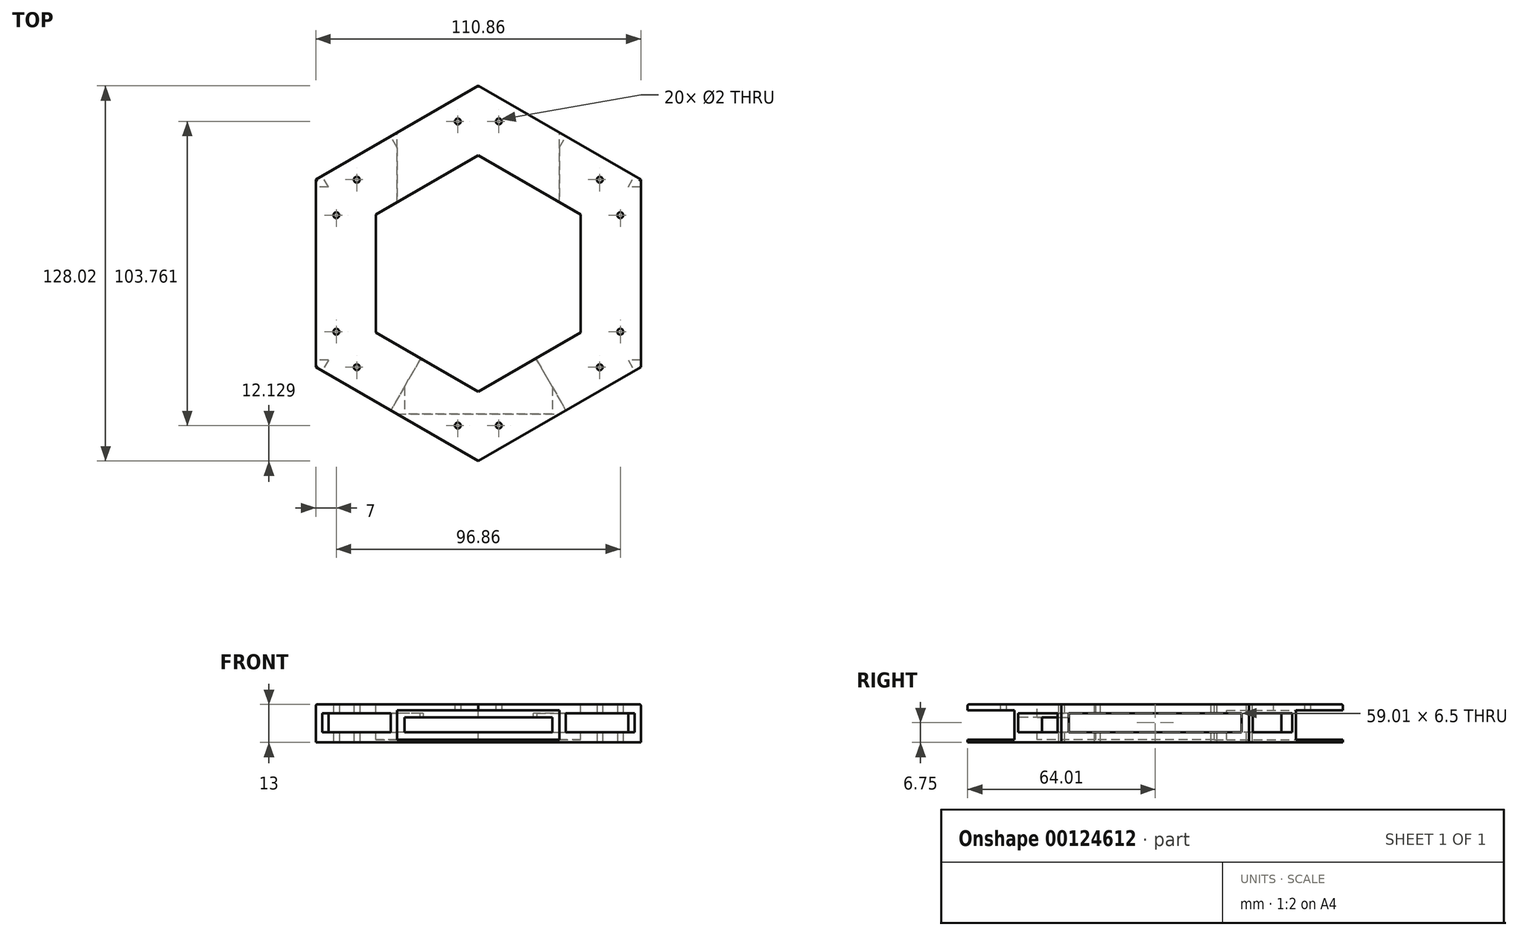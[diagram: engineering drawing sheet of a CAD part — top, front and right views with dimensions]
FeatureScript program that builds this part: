
annotation { "Feature Type Name" : "Feature", "Feature Type Description" : "" }
export const myFeature = defineFeature(function(context is Context, id is Id, definition is map)
    precondition{}
    {
        {
            var Q0;
            Q0=qCreatedBy(makeId("Top.planeOp"),FACE);
            var sketch = newSketch(context, id + "F0", { "sketchPlane" : qUnion([Q0])});
            skCircle(sketch, "E0.cCircle", {"center": v(0, 0) * mm, "radius": 55.43 * mm, "construction": true});
            skLineSegment(sketch, "E0.0", {"start": v(-55.43, -32) * mm, "end": v(-55.43, 32) * mm});
            skLineSegment(sketch, "E0.1", {"start": v(-55.43, 32) * mm, "end": v(0, 64) * mm});
            skLineSegment(sketch, "E0.2", {"start": v(0, 64) * mm, "end": v(55.43, 32) * mm});
            skLineSegment(sketch, "E0.3", {"start": v(55.43, 32) * mm, "end": v(55.43, -32) * mm});
            skLineSegment(sketch, "E0.4", {"start": v(55.43, -32) * mm, "end": v(0, -64) * mm});
            skLineSegment(sketch, "E0.5", {"start": v(0, -64) * mm, "end": v(-55.43, -32) * mm});
            skPoint(sketch, "E0.0.midPoint", {"position": v(-55.43, 0) * mm});
            skLineSegment(sketch, "E1", {"start": v(-55.43, -32) * mm, "end": v(0, 0) * mm});
            skLineSegment(sketch, "E2", {"start": v(-55.43, 32) * mm, "end": v(0, 0) * mm});
            skLineSegment(sketch, "E3.0", {"start": v(-48.43, -19.88) * mm, "end": v(-48.43, 19.88) * mm});
            skLineSegment(sketch, "E3.1", {"start": v(-48.43, -19.88) * mm, "end": v(-14, 0) * mm});
            skLineSegment(sketch, "E3.2", {"start": v(-48.43, 19.88) * mm, "end": v(-14, 0) * mm});
            skCircle(sketch, "E4", {"center": v(-48.43, -19.88) * mm, "radius": 1 * mm});
            skCircle(sketch, "E5", {"center": v(-48.43, 19.88) * mm, "radius": 1 * mm});
            skCircle(sketch, "E6.1.0", {"center": v(-7, -51.88) * mm, "radius": 1 * mm});
            skCircle(sketch, "E6.1.1", {"center": v(-41.43, -32) * mm, "radius": 1 * mm});
            skCircle(sketch, "E6.2.0", {"center": v(41.43, -32) * mm, "radius": 1 * mm});
            skCircle(sketch, "E6.2.1", {"center": v(7, -51.88) * mm, "radius": 1 * mm});
            skCircle(sketch, "E6.3.0", {"center": v(48.43, 19.88) * mm, "radius": 1 * mm});
            skCircle(sketch, "E6.3.1", {"center": v(48.43, -19.88) * mm, "radius": 1 * mm});
            skCircle(sketch, "E6.4.0", {"center": v(7, 51.88) * mm, "radius": 1 * mm});
            skCircle(sketch, "E6.4.1", {"center": v(41.43, 32) * mm, "radius": 1 * mm});
            skCircle(sketch, "E6.5.0", {"center": v(-41.43, 32) * mm, "radius": 1 * mm});
            skCircle(sketch, "E6.5.1", {"center": v(-7, 51.88) * mm, "radius": 1 * mm});
            skSolve(sketch);
        }
        {
            var Q0;
            Q0=makeQuery(id+"F0.imprint","IMPRINT",FACE,{"disambiguationData":[TD([[makeQuery(id+"F0.imprint","IMPRINT",EDGE,{"derivedFrom":sQuery(id+"F0.wireOp",EDGE,"E0.1")}),-1.0]])]});
            var Q1;
            {var subQ0=sQuery(id+"F0.wireOp",EDGE,"E4");var subQ1=sQuery(id+"F0.wireOp",EDGE,"E3.0");var subQ2=makeQuery(id+"F0.imprint","INTERSECT",VERTEX,{"derivedFrom":[subQ1,subQ0]});Q1=makeQuery(id+"F0.imprint","IMPRINT",FACE,{"disambiguationData":[TD([[makeQuery(id+"F0.imprint","IMPRINT",EDGE,{"disambiguationData":[TD([[subQ2,-1.0]])],"derivedFrom":subQ1}),-1.0]])]});}
            var Q2;
            Q2=makeQuery(id+"F0.imprint","IMPRINT",FACE,{"disambiguationData":[TD([[makeQuery(id+"F0.imprint","IMPRINT",EDGE,{"derivedFrom":sQuery(id+"F0.wireOp",EDGE,"E0.0")}),-1.0]])]});
            extrude(context, id + "F1", {"entities" : qUnion([Q0, Q1, Q2]), "depth" : 2 * mm});
        }
        {
            var Q0;
            Q0=makeQuery(id+"F1.opExtrude","CAP_EDGE",EDGE,{"disambiguationData":[OSD([sQuery(id+"F0.wireOp",EDGE,"E0.0")])],"isStart":false});
            var Q1;
            Q1=makeQuery(id+"F1.opExtrude","CAP_EDGE",EDGE,{"disambiguationData":[OSD([sQuery(id+"F0.wireOp",EDGE,"E0.5")])],"isStart":false});
            var Q2;
            Q2=makeQuery(id+"F1.opExtrude","CAP_EDGE",EDGE,{"disambiguationData":[OSD([sQuery(id+"F0.wireOp",EDGE,"E0.1")])],"isStart":false});
            var Q3;
            Q3=makeQuery(id+"F1.opExtrude","CAP_EDGE",EDGE,{"disambiguationData":[OSD([sQuery(id+"F0.wireOp",EDGE,"E0.2")])],"isStart":false});
            var Q4;
            Q4=makeQuery(id+"F1.opExtrude","CAP_EDGE",EDGE,{"disambiguationData":[OSD([sQuery(id+"F0.wireOp",EDGE,"E0.3")])],"isStart":false});
            var Q5;
            Q5=makeQuery(id+"F1.opExtrude","CAP_EDGE",EDGE,{"disambiguationData":[OSD([sQuery(id+"F0.wireOp",EDGE,"E0.4")])],"isStart":false});
            fillet(context, id + "F2", {"entities" : qUnion([Q0, Q1, Q2, Q3, Q4, Q5]), "radius" : 0.5 * mm, "tangentPropagation" : true, "allowEdgeOverflow" : false});
        }
        {
            var Q0;
            Q0=makeQuery(id+"F1.opExtrude","CAP_FACE",FACE,{"disambiguationData":[OSD([sQuery(id+"F0.wireOp",EDGE,"E0.0"),sQuery(id+"F0.wireOp",EDGE,"E0.1"),sQuery(id+"F0.wireOp",EDGE,"E0.2"),sQuery(id+"F0.wireOp",EDGE,"E0.3"),sQuery(id+"F0.wireOp",EDGE,"E0.4"),sQuery(id+"F0.wireOp",EDGE,"E0.5"),sQuery(id+"F0.wireOp",EDGE,"E4"),sQuery(id+"F0.wireOp",EDGE,"E5"),sQuery(id+"F0.wireOp",EDGE,"E6.1.0"),sQuery(id+"F0.wireOp",EDGE,"E6.1.1"),sQuery(id+"F0.wireOp",EDGE,"E6.2.0"),sQuery(id+"F0.wireOp",EDGE,"E6.2.1"),sQuery(id+"F0.wireOp",EDGE,"E6.3.0"),sQuery(id+"F0.wireOp",EDGE,"E6.3.1"),sQuery(id+"F0.wireOp",EDGE,"E6.4.0"),sQuery(id+"F0.wireOp",EDGE,"E6.4.1"),sQuery(id+"F0.wireOp",EDGE,"E6.5.0"),sQuery(id+"F0.wireOp",EDGE,"E6.5.1")])],"isStart":false});
            var sketch = newSketch(context, id + "F3", { "sketchPlane" : qUnion([Q0])});
            skLineSegment(sketch, "E7.0", {"start": v(34.93, 20.17) * mm, "end": v(0, 40.33) * mm});
            skLineSegment(sketch, "E7.1", {"start": v(-34.93, 20.17) * mm, "end": v(-34.93, -20.17) * mm});
            skLineSegment(sketch, "E7.2", {"start": v(-34.93, -20.17) * mm, "end": v(0, -40.33) * mm});
            skLineSegment(sketch, "E7.3", {"start": v(0, 40.33) * mm, "end": v(-34.93, 20.17) * mm});
            skLineSegment(sketch, "E7.4", {"start": v(0, -40.33) * mm, "end": v(34.93, -20.17) * mm});
            skLineSegment(sketch, "E7.5", {"start": v(34.93, -20.17) * mm, "end": v(34.93, 20.17) * mm});
            skLineSegment(sketch, "E8.0", {"start": v(0, -69.2) * mm, "end": v(59.93, -34.6) * mm});
            skLineSegment(sketch, "E8.1", {"start": v(59.93, 34.6) * mm, "end": v(0, 69.2) * mm});
            skLineSegment(sketch, "E8.2", {"start": v(0, 69.2) * mm, "end": v(-59.93, 34.6) * mm});
            skLineSegment(sketch, "E8.3", {"start": v(59.93, -34.6) * mm, "end": v(59.93, 34.6) * mm});
            skLineSegment(sketch, "E8.4", {"start": v(-59.93, 34.6) * mm, "end": v(-59.93, -34.6) * mm});
            skLineSegment(sketch, "E8.5", {"start": v(-59.93, -34.6) * mm, "end": v(0, -69.2) * mm});
            skSolve(sketch);
        }
        {
            var Q0;
            Q0=makeQuery(id+"F3.imprint","IMPRINT",FACE,{"disambiguationData":[TD([[makeQuery(id+"F3.imprint","IMPRINT",EDGE,{"derivedFrom":sQuery(id+"F3.wireOp",EDGE,"E7.0")}),1.0]])]});
            extrude(context, id + "F4", {"entities" : qUnion([Q0]), "operationType" : NewBodyOperationType.REMOVE, "oppositeDirection" : true, "depth" : 25 * mm});
        }
        {
            var Q0;
            Q0=makeQuery(id+"F1.opExtrude","CAP_FACE",FACE,{"disambiguationData":[OSD([sQuery(id+"F0.wireOp",EDGE,"E0.0"),sQuery(id+"F0.wireOp",EDGE,"E0.1"),sQuery(id+"F0.wireOp",EDGE,"E0.2"),sQuery(id+"F0.wireOp",EDGE,"E0.3"),sQuery(id+"F0.wireOp",EDGE,"E0.4"),sQuery(id+"F0.wireOp",EDGE,"E0.5"),sQuery(id+"F0.wireOp",EDGE,"E4"),sQuery(id+"F0.wireOp",EDGE,"E5"),sQuery(id+"F0.wireOp",EDGE,"E6.1.0"),sQuery(id+"F0.wireOp",EDGE,"E6.1.1"),sQuery(id+"F0.wireOp",EDGE,"E6.2.0"),sQuery(id+"F0.wireOp",EDGE,"E6.2.1"),sQuery(id+"F0.wireOp",EDGE,"E6.3.0"),sQuery(id+"F0.wireOp",EDGE,"E6.3.1"),sQuery(id+"F0.wireOp",EDGE,"E6.4.0"),sQuery(id+"F0.wireOp",EDGE,"E6.4.1"),sQuery(id+"F0.wireOp",EDGE,"E6.5.0"),sQuery(id+"F0.wireOp",EDGE,"E6.5.1")])],"isStart":true});
            var sketch = newSketch(context, id + "F5", { "sketchPlane" : qUnion([Q0])});
            skLineSegment(sketch, "E9", {"start": v(-17.46, 30.25) * mm, "end": v(-27.71, 48) * mm});
            skLineSegment(sketch, "E10.1.0", {"start": v(-34.93, 0) * mm, "end": v(-55.43, 0) * mm});
            skLineSegment(sketch, "E10.2.0", {"start": v(-17.46, -30.25) * mm, "end": v(-27.72, -48) * mm});
            skLineSegment(sketch, "E10.3.0", {"start": v(17.46, -30.25) * mm, "end": v(27.71, -48) * mm});
            skLineSegment(sketch, "E10.4.0", {"start": v(34.93, 0) * mm, "end": v(55.43, 0) * mm});
            skLineSegment(sketch, "E10.5.0", {"start": v(17.46, 30.25) * mm, "end": v(27.72, 48) * mm});
            skPoint(sketch, "E10.center", {"position": v(0, 0) * mm});
            skLineSegment(sketch, "E11.bottom", {"start": v(-27.71, 48) * mm, "end": v(27.71, 48) * mm});
            skLineSegment(sketch, "E11.top", {"start": v(-27.71, -48) * mm, "end": v(27.71, -48) * mm});
            skLineSegment(sketch, "E11.left", {"start": v(-27.71, 48) * mm, "end": v(-27.71, -48) * mm});
            skLineSegment(sketch, "E11.right", {"start": v(27.71, 48) * mm, "end": v(27.71, -48) * mm});
            skPoint(sketch, "E12", {"position": v(-27.71, -24.33) * mm});
            skPoint(sketch, "E13", {"position": v(-27.71, 24.33) * mm});
            skPoint(sketch, "E14", {"position": v(27.71, 24.33) * mm});
            skPoint(sketch, "E15", {"position": v(27.71, -24.33) * mm});
            skSolve(sketch);
        }
        {
            var Q0;
            {var subQ10=sQuery(id+"F5.wireOp",EDGE,"E10.1.0");Q0=makeQuery(id+"F5.imprint","IMPRINT",FACE,{"disambiguationData":[TD([[makeQuery(id+"F5.imprint","IMPRINT",EDGE,{"derivedFrom":subQ10}),-1.0]])]});}
            var Q1;
            {var subQ6=sQuery(id+"F5.wireOp",EDGE,"E10.1.0");Q1=makeQuery(id+"F5.imprint","IMPRINT",FACE,{"disambiguationData":[TD([[makeQuery(id+"F5.imprint","IMPRINT",EDGE,{"derivedFrom":subQ6}),1.0]])]});}
            var Q2;
            {var subQ10=sQuery(id+"F5.wireOp",EDGE,"E10.4.0");Q2=makeQuery(id+"F5.imprint","IMPRINT",FACE,{"disambiguationData":[TD([[makeQuery(id+"F5.imprint","IMPRINT",EDGE,{"derivedFrom":subQ10}),-1.0]])]});}
            var Q3;
            {var subQ12=sQuery(id+"F5.wireOp",EDGE,"E10.4.0");Q3=makeQuery(id+"F5.imprint","IMPRINT",FACE,{"disambiguationData":[TD([[makeQuery(id+"F5.imprint","IMPRINT",EDGE,{"derivedFrom":subQ12}),1.0]])]});}
            var Q4;
            {var subQ4=sQuery(id+"F5.wireOp",EDGE,"E9");Q4=makeQuery(id+"F5.imprint","IMPRINT",FACE,{"disambiguationData":[TD([[makeQuery(id+"F5.imprint","IMPRINT",EDGE,{"derivedFrom":subQ4}),-1.0]])]});}
            var Q5;
            {var subQ0=sQuery(id+"F5.wireOp",EDGE,"E9");Q5=makeQuery(id+"F5.imprint","IMPRINT",FACE,{"disambiguationData":[TD([[makeQuery(id+"F5.imprint","IMPRINT",EDGE,{"derivedFrom":subQ0}),1.0]])]});}
            var Q6;
            {var subQ0=sQuery(id+"F5.wireOp",EDGE,"E10.5.0");Q6=makeQuery(id+"F5.imprint","IMPRINT",FACE,{"disambiguationData":[TD([[makeQuery(id+"F5.imprint","IMPRINT",EDGE,{"derivedFrom":subQ0}),-1.0]])]});}
            extrude(context, id + "F6", {"entities" : qUnion([Q0, Q1, Q2, Q3, Q4, Q5, Q6]), "operationType" : NewBodyOperationType.ADD, "depth" : 10 * mm});
        }
        {
            var Q0;
            {var subQ0=sQuery(id+"F0.wireOp",EDGE,"E0.0");Q0=makeQuery(id+"F6.boolean.opBoolean","MERGE",FACE,{"derivedFrom":[makeQuery(id+"F1.opExtrude","SWEPT_FACE",FACE,{"disambiguationData":[OSD([subQ0])]}),makeQuery(id+"F6.opExtrude","SWEPT_FACE",FACE,{"disambiguationData":[OSD([subQ0])]})]});}
            var sketch = newSketch(context, id + "F7", { "sketchPlane" : qUnion([Q0])});
            skLineSegment(sketch, "E16.0", {"start": v(29.5, -1) * mm, "end": v(-29.5, -1) * mm});
            skLineSegment(sketch, "E16.1", {"start": v(29.5, -1) * mm, "end": v(29.5, -7.5) * mm});
            skLineSegment(sketch, "E16.2", {"start": v(29.5, -7.5) * mm, "end": v(-29.5, -7.5) * mm});
            skLineSegment(sketch, "E16.3", {"start": v(-29.5, -1) * mm, "end": v(-29.5, -7.5) * mm});
            skSolve(sketch);
        }
        {
            var Q0;
            Q0=qSketchRegion(id+"F7",true);
            var Q1;
            Q1=makeQuery(id+"F7.imprint","IMPRINT",FACE,{"disambiguationData":[TD([[makeQuery(id+"F7.imprint","IMPRINT",EDGE,{"derivedFrom":sQuery(id+"F7.wireOp",EDGE,"E16.0")}),1.0]])]});
            extrude(context, id + "F8", {"entities" : qUnion([Q0, Q1]), "operationType" : NewBodyOperationType.REMOVE, "oppositeDirection" : true, "depth" : 127.9 * mm});
        }
        {
            var Q0;
            Q0=makeQuery(id+"F6.opExtrude","SWEPT_FACE",FACE,{"disambiguationData":[OSD([sQuery(id+"F5.wireOp",EDGE,"E11.bottom")])]});
            var sketch = newSketch(context, id + "F9", { "sketchPlane" : qUnion([Q0])});
            skLineSegment(sketch, "E17.0", {"start": v(25.21, -2.5) * mm, "end": v(-25.21, -2.5) * mm});
            skLineSegment(sketch, "E17.1", {"start": v(25.21, -7.5) * mm, "end": v(25.21, -2.5) * mm});
            skLineSegment(sketch, "E17.2", {"start": v(-25.21, -7.5) * mm, "end": v(25.21, -7.5) * mm});
            skLineSegment(sketch, "E17.3", {"start": v(-25.21, -2.5) * mm, "end": v(-25.21, -7.5) * mm});
            skSolve(sketch);
        }
        {
            var Q0;
            Q0=makeQuery(id+"F9.imprint","IMPRINT",FACE,{"disambiguationData":[TD([[makeQuery(id+"F9.imprint","IMPRINT",EDGE,{"derivedFrom":sQuery(id+"F9.wireOp",EDGE,"E17.0")}),1.0]])]});
            extrude(context, id + "F10", {"entities" : qUnion([Q0]), "operationType" : NewBodyOperationType.REMOVE, "oppositeDirection" : true, "depth" : 25 * mm});
        }
        {
            var Q0;
            {var subQ0=sQuery(id+"F0.wireOp",EDGE,"E0.2");Q0=makeQuery(id+"F6.boolean.opBoolean","MERGE",FACE,{"derivedFrom":[makeQuery(id+"F1.opExtrude","SWEPT_FACE",FACE,{"disambiguationData":[OSD([subQ0])]}),makeQuery(id+"F6.opExtrude","SWEPT_FACE",FACE,{"disambiguationData":[OSD([subQ0])]})]});}
            var sketch = newSketch(context, id + "F11", { "sketchPlane" : qUnion([Q0])});
            skLineSegment(sketch, "E18", {"start": v(0, 0) * mm, "end": v(0, 1.5) * mm});
            skLineSegment(sketch, "E19", {"start": v(0, 1.5) * mm, "end": v(-32, 1.5) * mm});
            skLineSegment(sketch, "E20.0", {"start": v(-2.5, -1) * mm, "end": v(-29.5, -1) * mm});
            skLineSegment(sketch, "E20.1", {"start": v(-2.5, -7.5) * mm, "end": v(-2.5, -1) * mm});
            skLineSegment(sketch, "E20.2", {"start": v(-2.5, -7.5) * mm, "end": v(-29.5, -7.5) * mm});
            skLineSegment(sketch, "E20.3", {"start": v(-29.5, -1) * mm, "end": v(-29.5, -7.5) * mm});
            skSolve(sketch);
        }
        {
            var Q0;
            Q0=makeQuery(id+"F11.imprint","IMPRINT",FACE,{"disambiguationData":[TD([[makeQuery(id+"F11.imprint","IMPRINT",EDGE,{"derivedFrom":sQuery(id+"F11.wireOp",EDGE,"E20.0")}),1.0]])]});
            extrude(context, id + "F12", {"entities" : qUnion([Q0]), "operationType" : NewBodyOperationType.REMOVE, "oppositeDirection" : true, "depth" : 25 * mm});
        }
        {
            var Q0;
            {var subQ0=sQuery(id+"F0.wireOp",EDGE,"E0.5");Q0=makeQuery(id+"F6.boolean.opBoolean","MERGE",FACE,{"derivedFrom":[makeQuery(id+"F1.opExtrude","SWEPT_FACE",FACE,{"disambiguationData":[OSD([subQ0])]}),makeQuery(id+"F6.opExtrude","SWEPT_FACE",FACE,{"disambiguationData":[OSD([subQ0])]})]});}
            var sketch = newSketch(context, id + "F13", { "sketchPlane" : qUnion([Q0])});
            skLineSegment(sketch, "E21", {"start": v(0, 0) * mm, "end": v(0, 1.5) * mm});
            skLineSegment(sketch, "E22", {"start": v(0, 1.5) * mm, "end": v(-32, 1.5) * mm});
            skLineSegment(sketch, "E23.0", {"start": v(-2.5, -1) * mm, "end": v(-29.5, -1) * mm});
            skLineSegment(sketch, "E23.1", {"start": v(-2.5, -7.5) * mm, "end": v(-2.5, -1) * mm});
            skLineSegment(sketch, "E23.2", {"start": v(-2.5, -7.5) * mm, "end": v(-29.5, -7.5) * mm});
            skLineSegment(sketch, "E23.3", {"start": v(-29.5, -1) * mm, "end": v(-29.5, -7.5) * mm});
            skSolve(sketch);
        }
        {
            var Q0;
            Q0=qSketchRegion(id+"F13",true);
            extrude(context, id + "F14", {"entities" : qUnion([Q0]), "operationType" : NewBodyOperationType.REMOVE, "oppositeDirection" : true, "depth" : 25 * mm});
        }
        {
            var Q0;
            {var subQ0=sQuery(id+"F0.wireOp",EDGE,"E0.4");Q0=makeQuery(id+"F6.boolean.opBoolean","MERGE",FACE,{"derivedFrom":[makeQuery(id+"F1.opExtrude","SWEPT_FACE",FACE,{"disambiguationData":[OSD([subQ0])]}),makeQuery(id+"F6.opExtrude","SWEPT_FACE",FACE,{"disambiguationData":[OSD([subQ0])]})]});}
            var sketch = newSketch(context, id + "F15", { "sketchPlane" : qUnion([Q0])});
            skLineSegment(sketch, "E24", {"start": v(0, 0) * mm, "end": v(0, 1.5) * mm});
            skLineSegment(sketch, "E25", {"start": v(0, 1.5) * mm, "end": v(32, 1.5) * mm});
            skLineSegment(sketch, "E26.0", {"start": v(2.5, -1) * mm, "end": v(29.5, -1) * mm});
            skLineSegment(sketch, "E26.1", {"start": v(2.5, -7.5) * mm, "end": v(2.5, -1) * mm});
            skLineSegment(sketch, "E26.2", {"start": v(29.5, -7.5) * mm, "end": v(2.5, -7.5) * mm});
            skLineSegment(sketch, "E26.3", {"start": v(29.5, -1) * mm, "end": v(29.5, -7.5) * mm});
            skSolve(sketch);
        }
        {
            var Q0;
            Q0=qSketchRegion(id+"F15",true);
            var Q1;
            Q1=makeQuery(id+"F15.imprint","IMPRINT",FACE,{"disambiguationData":[TD([[makeQuery(id+"F15.imprint","IMPRINT",EDGE,{"derivedFrom":sQuery(id+"F15.wireOp",EDGE,"E26.0")}),-1.0]])]});
            extrude(context, id + "F16", {"entities" : qUnion([Q0, Q1]), "operationType" : NewBodyOperationType.REMOVE, "oppositeDirection" : true, "depth" : 25 * mm});
        }
        {
            var Q0;
            {var subQ0=sQuery(id+"F0.wireOp",EDGE,"E0.1");Q0=makeQuery(id+"F6.boolean.opBoolean","MERGE",FACE,{"derivedFrom":[makeQuery(id+"F1.opExtrude","SWEPT_FACE",FACE,{"disambiguationData":[OSD([subQ0])]}),makeQuery(id+"F6.opExtrude","SWEPT_FACE",FACE,{"disambiguationData":[OSD([subQ0])]})]});}
            var sketch = newSketch(context, id + "F17", { "sketchPlane" : qUnion([Q0])});
            skLineSegment(sketch, "E27", {"start": v(0, 0) * mm, "end": v(0, 1.5) * mm});
            skLineSegment(sketch, "E28", {"start": v(0, 1.5) * mm, "end": v(32, 1.5) * mm});
            skLineSegment(sketch, "E29.0", {"start": v(2.5, -1) * mm, "end": v(29.5, -1) * mm});
            skLineSegment(sketch, "E29.1", {"start": v(2.5, -7.5) * mm, "end": v(2.5, -1) * mm});
            skLineSegment(sketch, "E29.2", {"start": v(29.5, -7.5) * mm, "end": v(2.5, -7.5) * mm});
            skLineSegment(sketch, "E29.3", {"start": v(29.5, -1) * mm, "end": v(29.5, -7.5) * mm});
            skSolve(sketch);
        }
        {
            var Q0;
            Q0=makeQuery(id+"F17.imprint","IMPRINT",FACE,{"disambiguationData":[TD([[makeQuery(id+"F17.imprint","IMPRINT",EDGE,{"derivedFrom":sQuery(id+"F17.wireOp",EDGE,"E29.0")}),-1.0]])]});
            extrude(context, id + "F18", {"entities" : qUnion([Q0]), "operationType" : NewBodyOperationType.REMOVE, "oppositeDirection" : true, "depth" : 25 * mm});
        }
        {
            var Q0;
            Q0=makeQuery(id+"F6.opExtrude","CAP_FACE",FACE,{"disambiguationData":[OSD([sQuery(id+"F0.wireOp",EDGE,"E0.0"),sQuery(id+"F0.wireOp",EDGE,"E0.1"),sQuery(id+"F0.wireOp",EDGE,"E0.2"),sQuery(id+"F0.wireOp",EDGE,"E0.3"),sQuery(id+"F0.wireOp",EDGE,"E0.4"),sQuery(id+"F0.wireOp",EDGE,"E0.5"),sQuery(id+"F0.wireOp",EDGE,"E4"),sQuery(id+"F0.wireOp",EDGE,"E5"),sQuery(id+"F0.wireOp",EDGE,"E6.1.0"),sQuery(id+"F0.wireOp",EDGE,"E6.1.1"),sQuery(id+"F0.wireOp",EDGE,"E6.2.0"),sQuery(id+"F0.wireOp",EDGE,"E6.2.1"),sQuery(id+"F0.wireOp",EDGE,"E6.3.0"),sQuery(id+"F0.wireOp",EDGE,"E6.3.1"),sQuery(id+"F0.wireOp",EDGE,"E6.4.0"),sQuery(id+"F0.wireOp",EDGE,"E6.4.1"),sQuery(id+"F0.wireOp",EDGE,"E6.5.0"),sQuery(id+"F0.wireOp",EDGE,"E6.5.1"),sQuery(id+"F3.wireOp",EDGE,"E7.0"),sQuery(id+"F3.wireOp",EDGE,"E7.1"),sQuery(id+"F3.wireOp",EDGE,"E7.2"),sQuery(id+"F3.wireOp",EDGE,"E7.3"),sQuery(id+"F3.wireOp",EDGE,"E7.4"),sQuery(id+"F3.wireOp",EDGE,"E7.5"),sQuery(id+"F5.wireOp",EDGE,"E11.bottom"),sQuery(id+"F5.wireOp",EDGE,"E11.left"),sQuery(id+"F5.wireOp",EDGE,"E11.right")])],"isStart":false});
            var sketch = newSketch(context, id + "F19", { "sketchPlane" : qUnion([Q0])});
            skCircle(sketch, "E30.cCircle", {"center": v(0, 0) * mm, "radius": 55.43 * mm, "construction": true});
            skLineSegment(sketch, "E30.0", {"start": v(-55.43, 32) * mm, "end": v(0, 64) * mm});
            skLineSegment(sketch, "E30.1", {"start": v(0, 64) * mm, "end": v(55.43, 32) * mm});
            skLineSegment(sketch, "E30.2", {"start": v(55.43, 32) * mm, "end": v(55.43, -32) * mm});
            skLineSegment(sketch, "E30.3", {"start": v(55.43, -32) * mm, "end": v(0, -64) * mm});
            skLineSegment(sketch, "E30.4", {"start": v(0, -64) * mm, "end": v(-55.43, -32) * mm});
            skLineSegment(sketch, "E30.5", {"start": v(-55.43, -32) * mm, "end": v(-55.43, 32) * mm});
            skPoint(sketch, "E30.0.midPoint", {"position": v(-27.71, 48) * mm});
            skSolve(sketch);
        }
        {
            var Q0;
            Q0=qSketchRegion(id+"F19",true);
            extrude(context, id + "F20", {"entities" : qUnion([Q0]), "operationType" : NewBodyOperationType.ADD, "depth" : 1 * mm});
        }
        {
            var Q0;
            {var subQ0=sQuery(id+"F0.wireOp",EDGE,"E6.5.0");Q0=makeQuery(id+"F20.boolean.opBoolean","SPLIT",FACE,{"disambiguationData":[TD([makeQuery(id+"F1.opExtrude","SWEPT_FACE",FACE,{"disambiguationData":[OSD([subQ0])]})])],"derivedFrom":makeQuery(id+"F20.opExtrude","CAP_FACE",FACE,{"disambiguationData":[OSD([sQuery(id+"F19.wireOp",EDGE,"E30.0"),sQuery(id+"F19.wireOp",EDGE,"E30.1"),sQuery(id+"F19.wireOp",EDGE,"E30.2"),sQuery(id+"F19.wireOp",EDGE,"E30.3"),sQuery(id+"F19.wireOp",EDGE,"E30.4"),sQuery(id+"F19.wireOp",EDGE,"E30.5")])],"isStart":true})});}
            var Q1;
            {var subQ0=sQuery(id+"F0.wireOp",EDGE,"E5");Q1=makeQuery(id+"F20.boolean.opBoolean","SPLIT",FACE,{"disambiguationData":[TD([makeQuery(id+"F1.opExtrude","SWEPT_FACE",FACE,{"disambiguationData":[OSD([subQ0])]})])],"derivedFrom":makeQuery(id+"F20.opExtrude","CAP_FACE",FACE,{"disambiguationData":[OSD([sQuery(id+"F19.wireOp",EDGE,"E30.0"),sQuery(id+"F19.wireOp",EDGE,"E30.1"),sQuery(id+"F19.wireOp",EDGE,"E30.2"),sQuery(id+"F19.wireOp",EDGE,"E30.3"),sQuery(id+"F19.wireOp",EDGE,"E30.4"),sQuery(id+"F19.wireOp",EDGE,"E30.5")])],"isStart":true})});}
            var Q2;
            {var subQ0=sQuery(id+"F0.wireOp",EDGE,"E4");Q2=makeQuery(id+"F20.boolean.opBoolean","SPLIT",FACE,{"disambiguationData":[TD([makeQuery(id+"F1.opExtrude","SWEPT_FACE",FACE,{"disambiguationData":[OSD([subQ0])]})])],"derivedFrom":makeQuery(id+"F20.opExtrude","CAP_FACE",FACE,{"disambiguationData":[OSD([sQuery(id+"F19.wireOp",EDGE,"E30.0"),sQuery(id+"F19.wireOp",EDGE,"E30.1"),sQuery(id+"F19.wireOp",EDGE,"E30.2"),sQuery(id+"F19.wireOp",EDGE,"E30.3"),sQuery(id+"F19.wireOp",EDGE,"E30.4"),sQuery(id+"F19.wireOp",EDGE,"E30.5")])],"isStart":true})});}
            var Q3;
            {var subQ0=sQuery(id+"F0.wireOp",EDGE,"E6.1.1");Q3=makeQuery(id+"F20.boolean.opBoolean","SPLIT",FACE,{"disambiguationData":[TD([makeQuery(id+"F1.opExtrude","SWEPT_FACE",FACE,{"disambiguationData":[OSD([subQ0])]})])],"derivedFrom":makeQuery(id+"F20.opExtrude","CAP_FACE",FACE,{"disambiguationData":[OSD([sQuery(id+"F19.wireOp",EDGE,"E30.0"),sQuery(id+"F19.wireOp",EDGE,"E30.1"),sQuery(id+"F19.wireOp",EDGE,"E30.2"),sQuery(id+"F19.wireOp",EDGE,"E30.3"),sQuery(id+"F19.wireOp",EDGE,"E30.4"),sQuery(id+"F19.wireOp",EDGE,"E30.5")])],"isStart":true})});}
            var Q4;
            {var subQ0=sQuery(id+"F0.wireOp",EDGE,"E6.2.0");Q4=makeQuery(id+"F20.boolean.opBoolean","SPLIT",FACE,{"disambiguationData":[TD([makeQuery(id+"F1.opExtrude","SWEPT_FACE",FACE,{"disambiguationData":[OSD([subQ0])]})])],"derivedFrom":makeQuery(id+"F20.opExtrude","CAP_FACE",FACE,{"disambiguationData":[OSD([sQuery(id+"F19.wireOp",EDGE,"E30.0"),sQuery(id+"F19.wireOp",EDGE,"E30.1"),sQuery(id+"F19.wireOp",EDGE,"E30.2"),sQuery(id+"F19.wireOp",EDGE,"E30.3"),sQuery(id+"F19.wireOp",EDGE,"E30.4"),sQuery(id+"F19.wireOp",EDGE,"E30.5")])],"isStart":true})});}
            var Q5;
            {var subQ0=sQuery(id+"F0.wireOp",EDGE,"E6.3.1");Q5=makeQuery(id+"F20.boolean.opBoolean","SPLIT",FACE,{"disambiguationData":[TD([makeQuery(id+"F1.opExtrude","SWEPT_FACE",FACE,{"disambiguationData":[OSD([subQ0])]})])],"derivedFrom":makeQuery(id+"F20.opExtrude","CAP_FACE",FACE,{"disambiguationData":[OSD([sQuery(id+"F19.wireOp",EDGE,"E30.0"),sQuery(id+"F19.wireOp",EDGE,"E30.1"),sQuery(id+"F19.wireOp",EDGE,"E30.2"),sQuery(id+"F19.wireOp",EDGE,"E30.3"),sQuery(id+"F19.wireOp",EDGE,"E30.4"),sQuery(id+"F19.wireOp",EDGE,"E30.5")])],"isStart":true})});}
            var Q6;
            {var subQ0=sQuery(id+"F0.wireOp",EDGE,"E6.4.1");Q6=makeQuery(id+"F20.boolean.opBoolean","SPLIT",FACE,{"disambiguationData":[TD([makeQuery(id+"F1.opExtrude","SWEPT_FACE",FACE,{"disambiguationData":[OSD([subQ0])]})])],"derivedFrom":makeQuery(id+"F20.opExtrude","CAP_FACE",FACE,{"disambiguationData":[OSD([sQuery(id+"F19.wireOp",EDGE,"E30.0"),sQuery(id+"F19.wireOp",EDGE,"E30.1"),sQuery(id+"F19.wireOp",EDGE,"E30.2"),sQuery(id+"F19.wireOp",EDGE,"E30.3"),sQuery(id+"F19.wireOp",EDGE,"E30.4"),sQuery(id+"F19.wireOp",EDGE,"E30.5")])],"isStart":true})});}
            var Q7;
            {var subQ0=sQuery(id+"F0.wireOp",EDGE,"E6.3.0");Q7=makeQuery(id+"F20.boolean.opBoolean","SPLIT",FACE,{"disambiguationData":[TD([makeQuery(id+"F1.opExtrude","SWEPT_FACE",FACE,{"disambiguationData":[OSD([subQ0])]})])],"derivedFrom":makeQuery(id+"F20.opExtrude","CAP_FACE",FACE,{"disambiguationData":[OSD([sQuery(id+"F19.wireOp",EDGE,"E30.0"),sQuery(id+"F19.wireOp",EDGE,"E30.1"),sQuery(id+"F19.wireOp",EDGE,"E30.2"),sQuery(id+"F19.wireOp",EDGE,"E30.3"),sQuery(id+"F19.wireOp",EDGE,"E30.4"),sQuery(id+"F19.wireOp",EDGE,"E30.5")])],"isStart":true})});}
            extrude(context, id + "F21", {"entities" : qUnion([Q0, Q1, Q2, Q3, Q4, Q5, Q6, Q7]), "operationType" : NewBodyOperationType.REMOVE, "oppositeDirection" : true, "depth" : 25 * mm});
        }
    });
